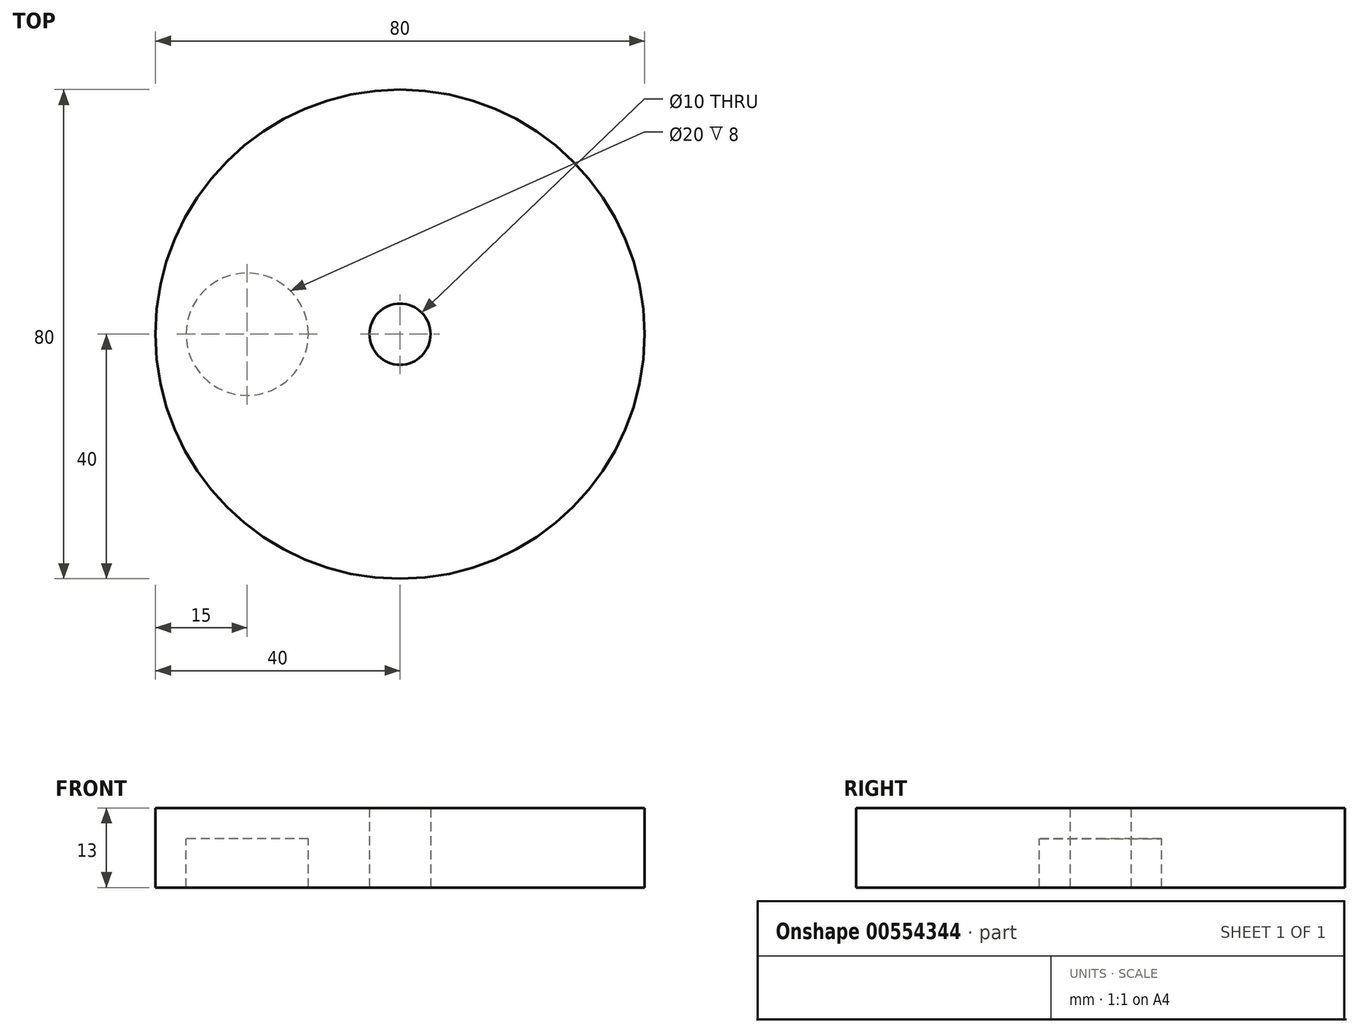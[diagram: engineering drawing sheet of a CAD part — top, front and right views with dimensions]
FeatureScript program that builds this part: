
annotation { "Feature Type Name" : "Feature", "Feature Type Description" : "" }
export const myFeature = defineFeature(function(context is Context, id is Id, definition is map)
    precondition{}
    {
        {
            var Q0;
            Q0=qCreatedBy(makeId("Top.planeOp"),FACE);
            var sketch = newSketch(context, id + "F0", { "sketchPlane" : qUnion([Q0])});
            skCircle(sketch, "E0", {"center": v(0, 0) * mm, "radius": 40 * mm});
            skCircle(sketch, "E1", {"center": v(0, 0) * mm, "radius": 5 * mm});
            skCircle(sketch, "E2", {"center": v(-25, 0) * mm, "radius": 10 * mm});
            skSolve(sketch);
        }
        {
            var Q0;
            Q0=makeQuery(id+"F0.imprint","IMPRINT",FACE,{"disambiguationData":[TD([[makeQuery(id+"F0.imprint","IMPRINT",EDGE,{"derivedFrom":sQuery(id+"F0.wireOp",EDGE,"E0")}),1.0]])]});
            var Q1;
            Q1=makeQuery(id+"F0.imprint","IMPRINT",FACE,{"disambiguationData":[TD([[makeQuery(id+"F0.imprint","IMPRINT",EDGE,{"derivedFrom":sQuery(id+"F0.wireOp",EDGE,"E2")}),1.0]])]});
            extrude(context, id + "F1", {"entities" : qUnion([Q0, Q1]), "depth" : 5 * mm, "offsetDistance" : 25 * mm});
        }
        {
            var Q0;
            Q0=makeQuery(id+"F0.imprint","IMPRINT",FACE,{"disambiguationData":[TD([[makeQuery(id+"F0.imprint","IMPRINT",EDGE,{"derivedFrom":sQuery(id+"F0.wireOp",EDGE,"E0")}),1.0]])]});
            extrude(context, id + "F2", {"entities" : qUnion([Q0]), "operationType" : NewBodyOperationType.ADD, "oppositeDirection" : true, "depth" : 8 * mm, "offsetDistance" : 25 * mm});
        }
    });
